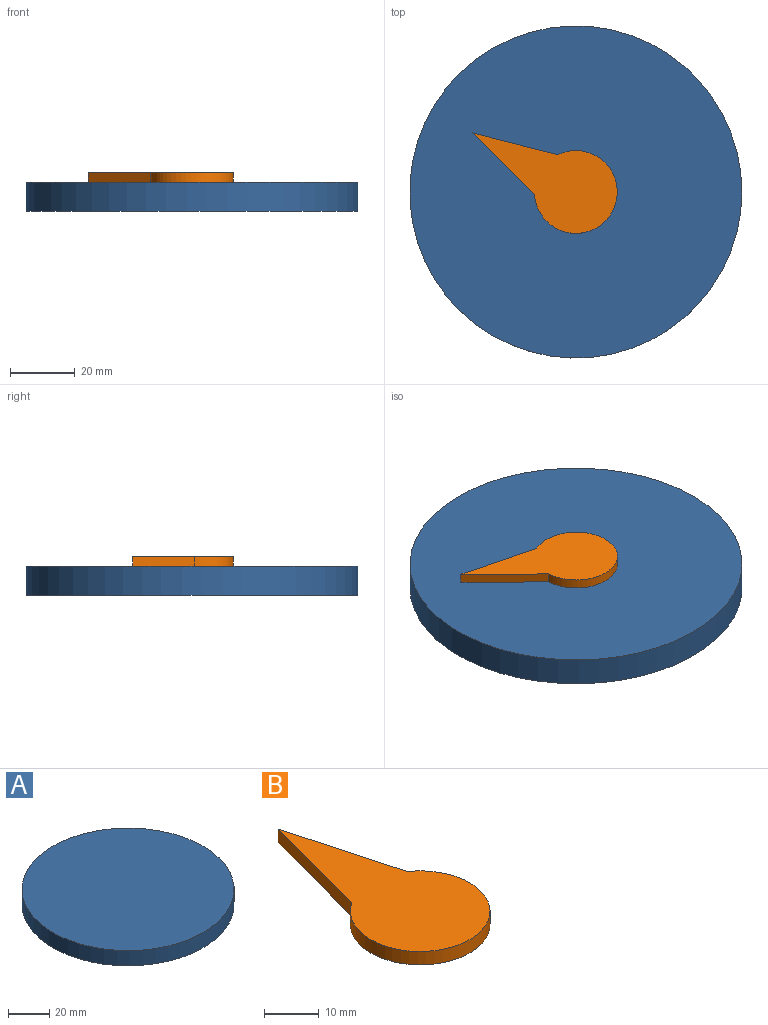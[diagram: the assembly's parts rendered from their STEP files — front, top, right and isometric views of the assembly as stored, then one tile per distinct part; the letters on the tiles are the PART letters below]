
ASSEMBLY  parts=2 mates=1
PART A: 3 faces, bbox 102.4x102.4x9 mm
  f0: cylinder r=51.18mm len=102.35mm, axis (0,0,-1), area 2894mm2, adj f1,f2
  f1: plane 102.35x102.35mm, normal (0,0,1), area 8228mm2, adj f0
  f2: plane 102.35x102.35mm, normal (0,0,-1), area 8228mm2, adj f0
PART B: 5 faces, bbox 25.5x49.6x3 mm
  f0: cylinder r=12.77mm len=25.55mm, axis (0,0,-1), area 195.9mm2, adj f1,f2,f3,f4
  f1: plane 26.21x7.17mm, normal (0.96,0.26,0), area 81.5mm2, adj f0,f2,f3,f4
  f2: plane 26.07x6.96mm, normal (-0.97,0.26,0), area 80.9mm2, adj f0,f1,f3,f4
  f3: plane 49.56x25.55mm, normal (0,0,1), area 676.7mm2, adj f0,f1,f2
  f4: plane 49.56x25.55mm, normal (0,0,-1), area 676.7mm2, adj f0,f1,f2
PLACE A at identity fixed
PLACE B rot(axis=(0,0,1),60.3deg) t=(0,0,0)mm
MATE revolute A.f0 <-> B.f0  axis (0,0,1) through (0,0,9)mm
